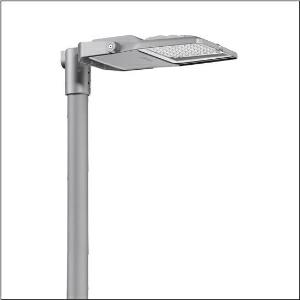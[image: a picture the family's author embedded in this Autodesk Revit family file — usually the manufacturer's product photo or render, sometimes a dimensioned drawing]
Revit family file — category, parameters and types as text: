
# Revit family: floodlight_fl_21_iq_mini___pl64_5xa7772c4e3a_b66a
name_source: partatom
category: Lighting Fixtures
units: mm (PartAtom-declared; Revit-internal decimal feet)

## family parameters
Cut with Voids When Loaded = No
Host = Face
Light Source = No
Part Type = Normal
Room Calculation Point = No
Round Connector Dimension = Use Diameter
Shared = No

## types (1)
- --- (1 x LED, 12280 lm, 87.2 W, 4000K)
    Apparent Load = 87 VA
    CIE Flux Codes = 28 80 98 100 100
    Color Rendering = 70
    Color Temperature = 4000K
    Default Elevation = 1800 mm
    Description = Floodlight FL 21 iQ mini, floodlight, primary light control with lens, of PMMA, primary optical cover: protective disc, of toughened safety glass, transparent, light distribution: PL64, light emission: direct distribution, installation type: surface-mounted, LED, High Power LED, rated luminous flux: 12.280lm, luminous efficacy: 141lm/W, light colour: 740, colour temperature: 4000K, control: Auto-Match, Temp-Guard, Night-Set, Smart-Wire, Desk-Remote (wireless, voltage-free reading and setting of iQ features in the workshop via application-optimized NFC function/RFID function), optimised constant luminous flux control (CLO 2.0), Light-Fading, Lumen-Switch, with terminal, 6-pole, mains connection: 220..240V, AC, 50/60Hz, start of lifetime: 87W, end of service life: 92W, reduction: 40W, luminaire housing, of diecast aluminium, powder-coated, Siteco® metallic grey (DB 702S), corrosivity category C5 mid according to DIN EN ISO 12944, sealing non-destructively replaceable, please order mast flange separately, mast bracket, of steel, galvanised, powder-coated, protection rating (complete): IP66, insulation class (complete): insulation class II (safety insulation), certification: CE, ENEC, VDE, protection symbol: D, impact resistance: IK08, permissible operating ambient temperature: -40..+40°C, permissible operating ambient temperature for outdoor applications: -40..+50°C, standard: DIN EN 12944, LABS conformity tested according to VDMA 24364:2018-05, packaging unit: 1 piece

Light Distribution: PL64
    Height = 70 mm
    Lamp = 1 x LED
    Lamp Light Flux = 12280 lm
    Lamp Power = 87.2 W
    Lamp count = 1
    Length = 485 mm
    Luminous efficacy = 141 lm/W
    Manufacturer = Siteco
    ModVariant = No
    Model = 5XA7772C4E3A
    Number of Poles = 1
    OnlyDefault = Yes
    Power Factor = 1
    Product Name = Floodlight FL 21 iQ mini | PL64
    Product group = floodlight | pylon annexe
    ProductGroupID = 6200
    Protection Class = Protection class II
    Protection Degree = IP 66
    RLX_Detail_Level = 1
    RLX_Emergency_Light_Flux = 0 lm
    RLX_Emergency_Type = 0
    RLX_Emergency_Type_DB = No
    RlxData = <blob elided: 101245 chars, md5=6373e688>
    Socket = socket
    Standby Power = 0 W
    System Light Flux = 12280 lm
    System Power = 87 W
    Type Comments = factory setting: luminous flux: 100 % | dim-lin: 254 | 456 mA
    Type Image = l_1007125.jpg
    URL = http://relux.com
    VarID = @adj_098517
    Voltage = 0 V
    Weight = 0.00 kg
    Width = 337 mm

## geometry (parser evidence)
native form markers: Blend x4, Sweep x13
no freeform markers — native parametric forms only
